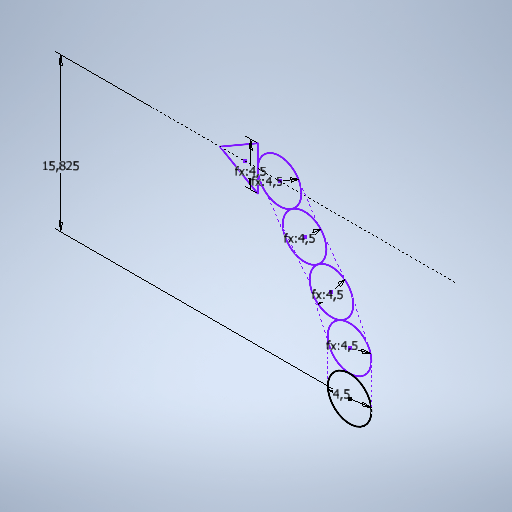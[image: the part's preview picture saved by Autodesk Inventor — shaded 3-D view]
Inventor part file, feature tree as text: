
AUTODESK INVENTOR PART (.ipt)
format: ipt  version: 2025.2 (Build 292293000, 293)  size: 273,920 bytes
history: native  units: mm
features: sketch x1
ambient origin geometry x8: Origin, YZ Plane, XZ Plane, XY Plane, X Axis, Y Axis, Z Axis, Center Point
feature tree (1):
  sketch  "Esboço1"  dims[d0=4.5mm d1=4.5mm d2=4.5mm d3=4.5mm d4=4.5mm d5=4.5mm d6=4.5mm d7=4.5mm d8=4.5mm d9=15.82528mm]
